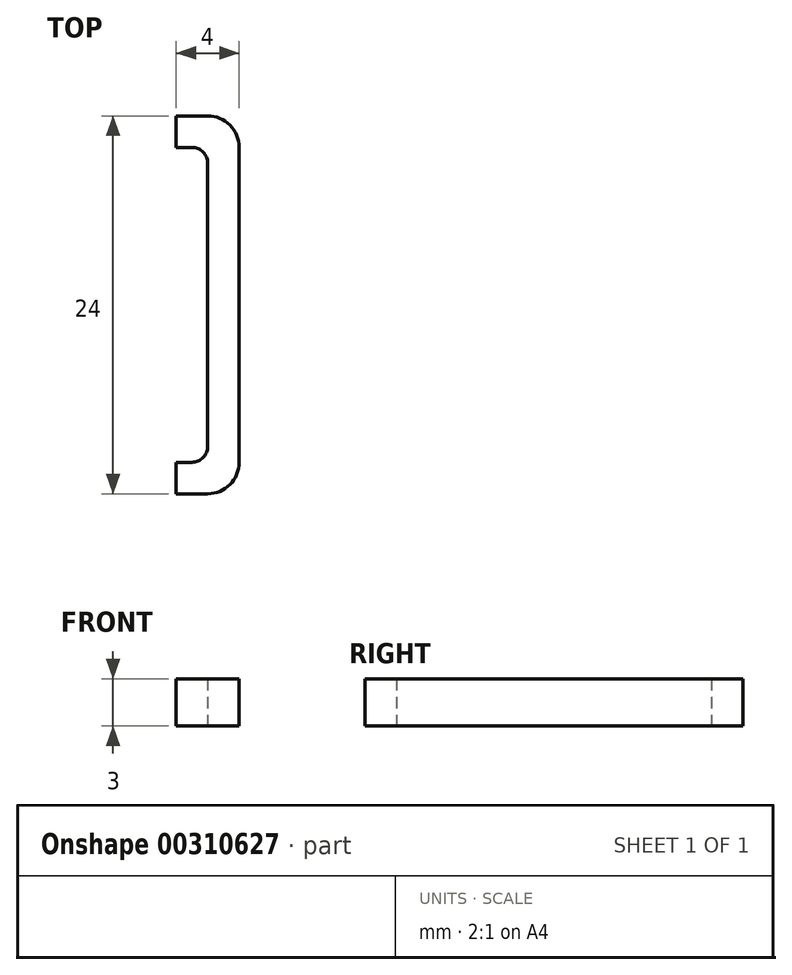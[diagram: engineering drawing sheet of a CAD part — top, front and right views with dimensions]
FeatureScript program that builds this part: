
annotation { "Feature Type Name" : "Feature", "Feature Type Description" : "" }
export const myFeature = defineFeature(function(context is Context, id is Id, definition is map)
    precondition{}
    {
        {
            var Q0;
            Q0=qCreatedBy(makeId("Top.planeOp"),FACE);
            var sketch = newSketch(context, id + "F0", { "sketchPlane" : qUnion([Q0])});
            skLineSegment(sketch, "E0.bottom", {"start": v(0, 12) * mm, "end": v(4, 12) * mm});
            skLineSegment(sketch, "E0.top", {"start": v(0, -12) * mm, "end": v(4, -12) * mm});
            skLineSegment(sketch, "E0.left", {"start": v(0, 12) * mm, "end": v(0, -12) * mm});
            skLineSegment(sketch, "E0.right", {"start": v(4, 12) * mm, "end": v(4, -12) * mm});
            skLineSegment(sketch, "E1.bottom", {"start": v(0, 10) * mm, "end": v(2, 10) * mm});
            skLineSegment(sketch, "E1.top", {"start": v(0, -10) * mm, "end": v(2, -10) * mm});
            skLineSegment(sketch, "E1.left", {"start": v(0, 10) * mm, "end": v(0, -10) * mm});
            skLineSegment(sketch, "E1.right", {"start": v(2, 10) * mm, "end": v(2, -10) * mm});
            skSolve(sketch);
        }
        {
            var Q0;
            {var subQ4=sQuery(id+"F0.wireOp",EDGE,"E0.bottom");Q0=makeQuery(id+"F0.imprint","IMPRINT",FACE,{"disambiguationData":[TD([[makeQuery(id+"F0.imprint","IMPRINT",EDGE,{"derivedFrom":subQ4}),-1.0]])]});}
            extrude(context, id + "F1", {"entities" : qUnion([Q0]), "endBound" : BoundingType.SYMMETRIC, "depth" : 3 * mm});
        }
        {
            var Q0;
            Q0=makeQuery(id+"F1.opExtrude","SWEPT_EDGE",EDGE,{"disambiguationData":[OSD([sQuery(id+"F0.wireOp",EDGE,"E0.top"),sQuery(id+"F0.wireOp",EDGE,"E0.right")])]});
            var Q1;
            Q1=makeQuery(id+"F1.opExtrude","SWEPT_EDGE",EDGE,{"disambiguationData":[OSD([sQuery(id+"F0.wireOp",EDGE,"E0.bottom"),sQuery(id+"F0.wireOp",EDGE,"E0.right")])]});
            fillet(context, id + "F2", {"entities" : qUnion([Q0, Q1]), "radius" : 2 * mm, "tangentPropagation" : true, "allowEdgeOverflow" : false});
        }
        {
            var Q0;
            Q0=makeQuery(id+"F1.opExtrude","SWEPT_EDGE",EDGE,{"disambiguationData":[OSD([sQuery(id+"F0.wireOp",EDGE,"E1.bottom"),sQuery(id+"F0.wireOp",EDGE,"E1.right")])]});
            var Q1;
            Q1=makeQuery(id+"F1.opExtrude","SWEPT_EDGE",EDGE,{"disambiguationData":[OSD([sQuery(id+"F0.wireOp",EDGE,"E1.top"),sQuery(id+"F0.wireOp",EDGE,"E1.right")])]});
            fillet(context, id + "F3", {"entities" : qUnion([Q0, Q1]), "radius" : 1 * mm, "tangentPropagation" : true, "allowEdgeOverflow" : false});
        }
    });
